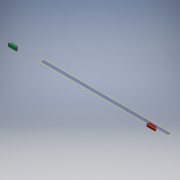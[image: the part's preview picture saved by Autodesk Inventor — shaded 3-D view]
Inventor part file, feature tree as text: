
AUTODESK INVENTOR PART (.ipt)
format: ipt  version: 2018 (Build 220112000, 112)  size: 138,752 bytes
history: native  units: in
note: dims shown in document units (in); Inventor stores cm internally (conversion verified against a paired STEP export)
features: reference x14, sketch x4, extrude x4, plane x3, other x3, projected_geometry x2
ambient origin geometry x8: Origin, YZ Plane, XZ Plane, XY Plane, X Axis, Y Axis, Z Axis, Center Point
bodies: Solid1 (feature_tree), Solid2 (feature_tree)
feature tree (30):
  plane  "Work Plane1"
  sketch  "Sketch2"  dims[d0=1.0in d1=0.0in d2=0.005in d3=0.0in]
  plane  "Work Plane2"
  extrude  "Extrusion1"  Depth=0.005in TaperAngle=0.0deg
  extrude  "Extrusion2"  Depth=0.005in TaperAngle=0.0deg
  sketch  "Sketch5"
  plane  "Work Plane3"
  extrude  "Extrusion3"  [1 undecoded]
  extrude  "Extrusion4"  [1 undecoded]
  reference  "Reference1"
  reference  "Reference2"
  reference  "Reference3"
  reference  "Reference4"
  reference  "Reference5"
  reference  "Reference6"
  reference  "Reference7"
  sketch  "Sketch3"  dims[d4=0.005in d5=0.0in d6=0.005in d7=0.0in]
  projected_geometry  "Projected Loop1"
  reference  "Reference8"
  reference  "Reference9"
  reference  "Reference10"
  reference  "Reference11"
  reference  "Reference12"
  reference  "Reference13"
  reference  "Reference14"
  sketch  "Sketch6"
  projected_geometry  "Projected Loop2"
  other  "<userpath>\Documents\Commodore Cube Project\Case\Assembly.iam"
  other  "Assembly.iam"
  other  "Tray:1"
note: 2 required parameter values undecoded (feature->parameter linkage not recoverable at this tier; creation-order binding heuristic only, values carry confidence <= 0.55)
